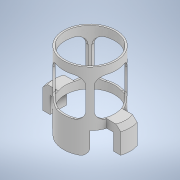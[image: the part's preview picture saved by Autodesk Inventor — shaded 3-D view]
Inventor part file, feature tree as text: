
AUTODESK INVENTOR PART (.ipt)
format: ipt  version: 2020 (Build 240168000, 168)  size: 279,552 bytes
history: native  units: in
note: dims shown in document units (in); Inventor stores cm internally (conversion verified against a paired STEP export)
features: sketch x7, extrude x6, chamfer x2, pattern_circular x1, fillet x1, hole x1, mirror x1
ambient origin geometry x8: Origin, YZ Plane, XZ Plane, XY Plane, X Axis, Y Axis, Z Axis, Center Point
bodies: Solid1 (feature_tree)
feature tree (19):
  extrude  "Extrusion1"  Depth=3.937in TaperAngle=0.0deg
  extrude  "Extrusion2"  Depth=3.937in TaperAngle=0.0deg
  extrude  "Extrusion3"  Depth=2.7559in
  pattern_circular  "Circular Pattern1"  Count=10  [1 undecoded]
  extrude  "Extrusion4"  TaperAngle=45.0deg  [1 undecoded]
  fillet  "Fillet1"  Radius=1.5748in
  extrude  "Extrusion5"  Depth=1.1811in
  chamfer  "Chamfer1"  Distance=0.9843in
  extrude  "Extrusion6"  Depth=0.0787in TaperAngle=0.0deg
  hole  "Hole2"  [1 undecoded]
  mirror  "Mirror1"
  chamfer  "Chamfer2"  Distance=0.0787in Angle=45.0deg
  sketch  "Sketch1"  dims[d0=3.7795in d1=3.937in d2=0.0in]
  sketch  "Sketch2"  dims[d3=3.5433in d4=3.937in d5=0.0in]
  sketch  "Sketch3"  dims[d6=2.3622in d7=2.7559in]
  sketch  "Sketch4"  dims[d8=0.5906in d9=3.937in d10=0.0in]
  sketch  "Sketch5"  dims[d11=1.5748in d12=360.0deg d15=45.0deg d16=1.5748in d17=0.0in]
  sketch  "Sketch6"  dims[d18=0.5512in d19=1.1811in d20=0.9843in d21=0.0in]
  sketch  "Sketch7"  dims[d22=0.315in d23=0.0787in d24=45.0deg d25=1.1811in d26=0.0in d27=0.1575in d35=0.1575in d36=0.2362in d37=0.1575in d38=0.0787in d39=90.0deg d40=0.2362in d41=0.0in d42=0.315in d43=0.0787in d44=45.0deg]
note: 3 required parameter values undecoded (feature->parameter linkage not recoverable at this tier; creation-order binding heuristic only, values carry confidence <= 0.55)
